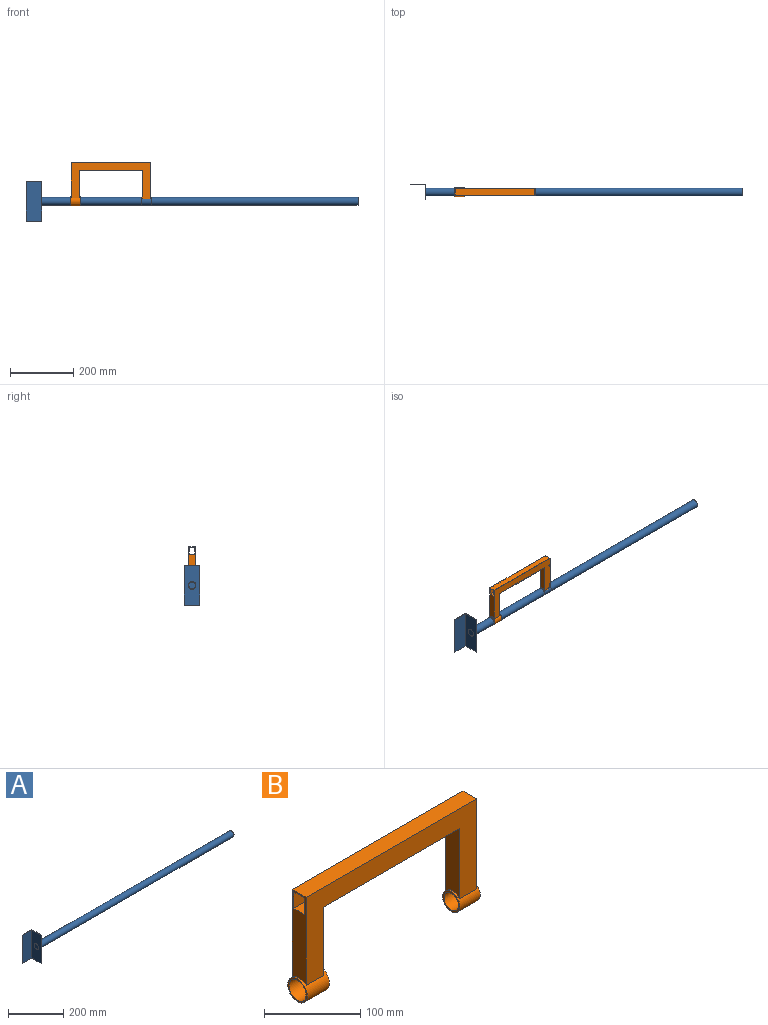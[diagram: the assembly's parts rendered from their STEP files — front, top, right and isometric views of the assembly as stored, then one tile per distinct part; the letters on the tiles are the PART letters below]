
ASSEMBLY  parts=2 mates=1
PART A: 12 faces, bbox 1050x50x125 mm
  f0: plane 125x2mm, normal (0,-1,0), area 250mm2, adj f1,f5,f6,f7
  f1: plane 125x50mm, normal (1,0,0), area 5759.1mm2, adj f0,f2,f6,f7,f9
  f2: plane 125x50mm, normal (0,1,0), area 6250mm2, adj f1,f3,f6,f7
  f3: plane 125x2mm, normal (-1,0,0), area 250mm2, adj f2,f4,f6,f7
  f4: plane 125x48mm, normal (0,-1,0), area 6000mm2, adj f3,f5,f6,f7
  f5: plane 125x48mm, normal (-1,0,0), area 6000mm2, adj f0,f4,f6,f7
  f6: plane 50x50mm, normal (0,0,1), area 196mm2, adj f0,f1,f2,f3,f4,f5
  f7: plane 50x50mm, normal (0,0,-1), area 196mm2, adj f0,f1,f2,f3,f4,f5
  f8: cylinder r=10.5mm len=1000mm, axis (-1,0,0), area 65973.4mm2, adj f10,f11
  f9: cylinder r=12.5mm len=1000mm, axis (-1,0,0), area 78539.8mm2, adj f1,f10
  f10: plane 25x25mm, normal (1,0,0), area 144.5mm2, adj f8,f9
  f11: plane 21x21mm, normal (1,0,0), area 346.4mm2, adj f8
PART B: 26 faces, bbox 255.3x28.7x136.2 mm
  f0: plane 89.35x20mm, normal (-1,0,0), area 1716.7mm2, adj f1,f4,f5,f11
  f1: cylinder r=12.5mm len=30mm, axis (-1,0,0), area 1776.6mm2, adj f0,f2,f3,f4,f5,f6
  f2: plane 25x25mm, normal (1,0,0), area 144.5mm2, adj f1,f7
  f3: plane 25x25mm, normal (-1,0,0), area 144.5mm2, adj f1,f7
  f4: plane 250x114.35mm, normal (0,-1,0), area 10648.5mm2, adj f0,f1,f6,f8,f10,f11,f15,f17
  f5: plane 250x114.3mm, normal (0,1,0), area 10646.3mm2, adj f0,f1,f6,f8,f10,f11,f15,f17
  f6: plane 114.35x20mm, normal (1,0,0), area 1880.7mm2, adj f1,f4,f5,f9,f10,f12,f13,f14
  f7: cylinder r=10.5mm len=30mm, axis (-1,0,0), area 1979.2mm2, adj f2,f3
  f8: plane 111.59x20mm, normal (-1,0,0), area 1839.4mm2, adj f4,f5,f9,f10,f12,f13,f14,f17
  f9: plane 250x21mm, normal (0,-1,0), area 5250mm2, adj f6,f8,f12,f14
  f10: plane 250x20mm, normal (0,0,1), area 5000mm2, adj f4,f5,f6,f8
  f11: plane 200x20mm, normal (0,0,-1), area 4000mm2, adj f0,f4,f5,f15
  f12: plane 250x16mm, normal (0,0,-1), area 4000mm2, adj f6,f8,f9,f13
  f13: plane 250x21mm, normal (0,1,0), area 5250mm2, adj f6,f8,f12,f14
  f14: plane 250x16mm, normal (0,0,1), area 4000mm2, adj f6,f8,f9,f13
  f15: plane 86.59x20mm, normal (1,0,0), area 1675.4mm2, adj f4,f5,f11,f17
  f16: cylinder r=12.5mm len=32.5mm, axis (-1,0,0), area 2552.5mm2, adj f18,f19
  f17: cylinder r=14.33mm len=32.5mm, axis (-1,0,0), area 2372.2mm2, adj f4,f5,f8,f15,f18,f19
  f18: plane 28.65x28.65mm, normal (1,0,0), area 154mm2, adj f16,f17
  f19: plane 28.65x28.65mm, normal (-1,0,0), area 154mm2, adj f16,f17
  f20: cylinder r=12.5mm len=21mm, axis (-1,0,0), area 364.6mm2, adj f21,f22,f23,f24
  f21: plane 87.21x21mm, normal (0,-1,0), area 1831.3mm2, adj f20,f22,f24,f25
  f22: plane 87.24x16mm, normal (-1,0,0), area 1363.9mm2, adj f20,f21,f23,f25
  f23: plane 87.24x21mm, normal (0,1,0), area 1832mm2, adj f20,f22,f24,f25
  f24: plane 87.24x16mm, normal (1,0,0), area 1363.9mm2, adj f20,f21,f23,f25
  f25: plane 21x16mm, normal (0,0,-1), area 336mm2, adj f21,f22,f23,f24
PLACE A t=(-274.52,15.59,38.41)mm
PLACE B t=(90.27,-4.61,125.91)mm
MATE cylindrical A.f8 <-> B.f16  axis (-1,0,0) through (-225.31,-4.61,125.91)mm
